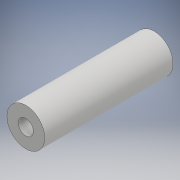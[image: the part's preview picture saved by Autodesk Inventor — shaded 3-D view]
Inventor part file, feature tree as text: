
AUTODESK INVENTOR PART (.ipt)
format: ipt  version: 2018 (Build 220112000, 112)  size: 95,232 bytes
history: native  units: mm
features: extrude x1, sketch x1
ambient origin geometry x8: Origin, YZ Plane, XZ Plane, XY Plane, X Axis, Y Axis, Z Axis, Center Point
bodies: Solid1 (feature_tree)
feature tree (2):
  extrude  "Extrusion1"  Depth=34.0mm
  sketch  "Sketch1"  dims[d0=10.0mm d1=4.0mm d2=34.0mm d3=0.0mm]
